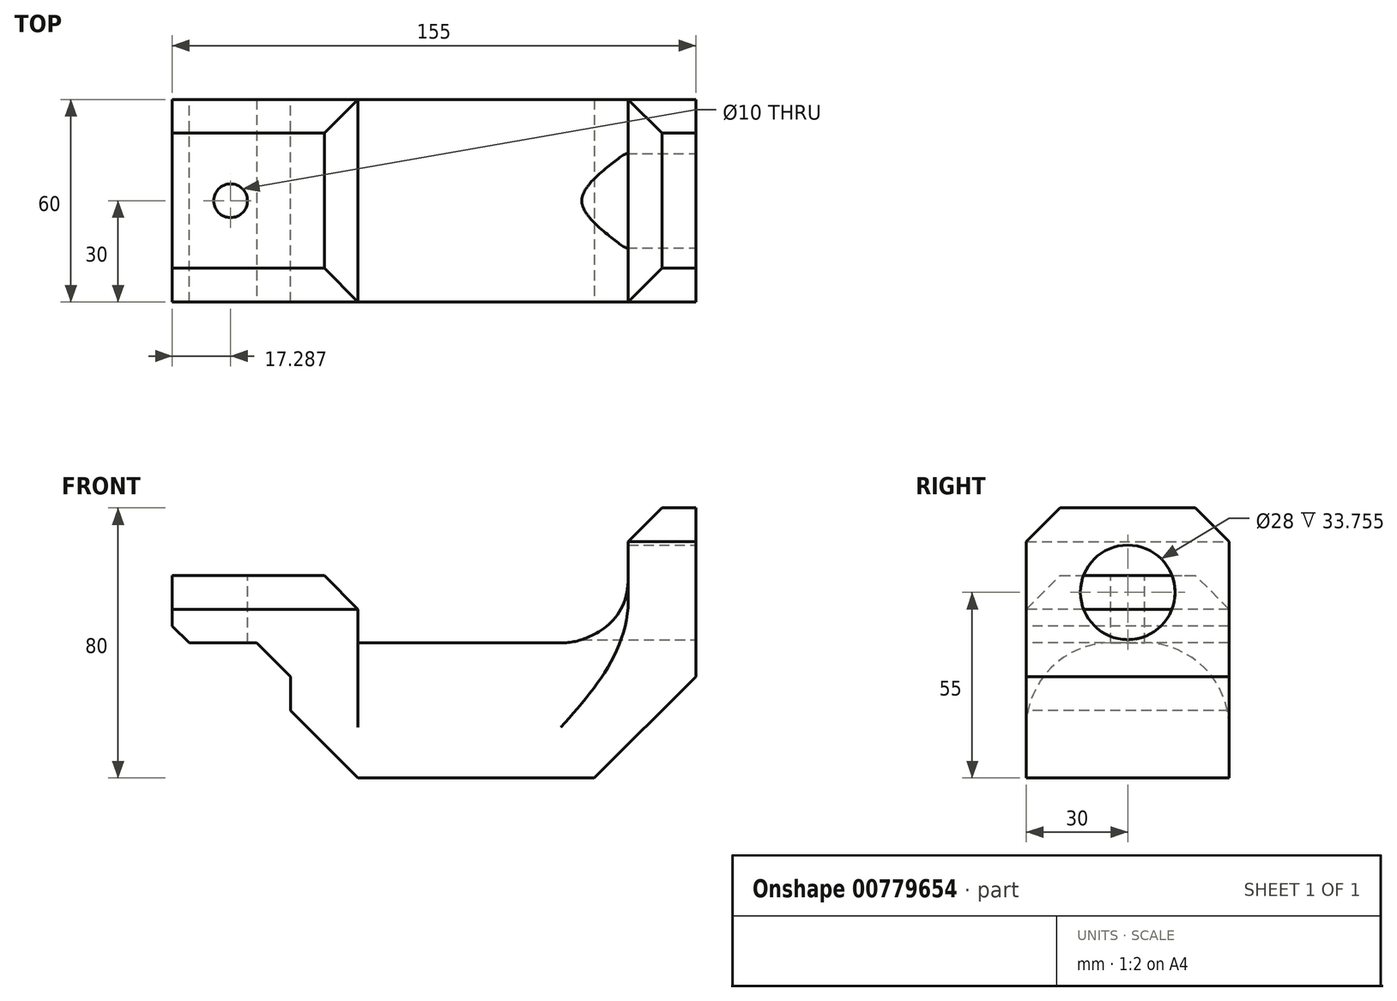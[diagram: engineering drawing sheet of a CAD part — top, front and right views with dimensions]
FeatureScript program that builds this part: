
annotation { "Feature Type Name" : "Feature", "Feature Type Description" : "" }
export const myFeature = defineFeature(function(context is Context, id is Id, definition is map)
    precondition{}
    {
        {
            var Q0;
            Q0=qCreatedBy(makeId("Front.planeOp"),FACE);
            var sketch = newSketch(context, id + "F0", { "sketchPlane" : qUnion([Q0])});
            skLineSegment(sketch, "E0.bottom", {"start": v(40, 20) * mm, "end": v(-40, 20) * mm});
            skLineSegment(sketch, "E0.top", {"start": v(40, -20) * mm, "end": v(-40, -20) * mm});
            skLineSegment(sketch, "E0.left", {"start": v(40, 20) * mm, "end": v(40, -20) * mm});
            skLineSegment(sketch, "E0.right", {"start": v(-40, 20) * mm, "end": v(-40, -20) * mm});
            skPoint(sketch, "E0.middle", {"position": v(0, 0) * mm});
            skLineSegment(sketch, "E1.bottom", {"start": v(-40, -20) * mm, "end": v(-60, -20) * mm});
            skLineSegment(sketch, "E1.top", {"start": v(-40, 40) * mm, "end": v(-60, 40) * mm});
            skLineSegment(sketch, "E1.left", {"start": v(-40, -20) * mm, "end": v(-40, 40) * mm});
            skLineSegment(sketch, "E1.right", {"start": v(-60, -20) * mm, "end": v(-60, 40) * mm});
            skLineSegment(sketch, "E2.bottom", {"start": v(-60, 40) * mm, "end": v(-80, 40) * mm});
            skLineSegment(sketch, "E2.top", {"start": v(-60, 20) * mm, "end": v(-80, 20) * mm});
            skLineSegment(sketch, "E2.left", {"start": v(-60, 40) * mm, "end": v(-60, 20) * mm});
            skLineSegment(sketch, "E3.bottom", {"start": v(-80, 40) * mm, "end": v(-95, 40) * mm});
            skLineSegment(sketch, "E3.top", {"start": v(-80, 20) * mm, "end": v(-95, 20) * mm});
            skLineSegment(sketch, "E3.right", {"start": v(-95, 40) * mm, "end": v(-95, 20) * mm});
            skLineSegment(sketch, "E4.bottom", {"start": v(40, -20) * mm, "end": v(60, -20) * mm});
            skLineSegment(sketch, "E4.top", {"start": v(40, 60) * mm, "end": v(60, 60) * mm});
            skLineSegment(sketch, "E4.left", {"start": v(40, -20) * mm, "end": v(40, 60) * mm});
            skLineSegment(sketch, "E4.right", {"start": v(60, -20) * mm, "end": v(60, 60) * mm});
            skSolve(sketch);
        }
        {
            var Q0;
            Q0 = qSketchRegion(id + "F0", true);
            extrude(context, id + "F1", {"entities" : qUnion([Q0]), "depth" : 60 * mm, "offsetDistance" : 25 * mm});
        }
        {
            var Q0;
            Q0=makeQuery(id+"F1.opExtrude","CAP_EDGE",EDGE,{"disambiguationData":[OSD([sQuery(id+"F0.wireOp",EDGE,"E0.bottom")])],"isStart":false});
            var Q1;
            Q1=makeQuery(id+"F1.opExtrude","CAP_EDGE",EDGE,{"disambiguationData":[OSD([sQuery(id+"F0.wireOp",EDGE,"E0.bottom")])],"isStart":true});
            fillet(context, id + "F2", {"entities" : qUnion([Q0, Q1]), "radius" : 25 * mm, "tangentPropagation" : true, "allowEdgeOverflow" : false});
        }
        {
            var Q0;
            Q0=makeQuery(id+"F1.opExtrude","SWEPT_FACE",FACE,{"disambiguationData":[OSD([sQuery(id+"F0.wireOp",EDGE,"E1.top"),sQuery(id+"F0.wireOp",EDGE,"E2.bottom"),sQuery(id+"F0.wireOp",EDGE,"E3.bottom")])]});
            var sketch = newSketch(context, id + "F3", { "sketchPlane" : qUnion([Q0])});
            skLineSegment(sketch, "E5", {"start": v(-60.43, -60) * mm, "end": v(-95, 0) * mm});
            skLineSegment(sketch, "E6", {"start": v(-95, 0) * mm, "end": v(-60.43, -60) * mm});
            skLineSegment(sketch, "E7", {"start": v(-60.43, 0) * mm, "end": v(-95, -60) * mm});
            skPoint(sketch, "E8", {"position": v(-77.71, -30) * mm});
            skSolve(sketch);
        }
        {
            var Q0;
            Q0=sQuery(id+"F3.wireOp",VERTEX,"E8");
            var Q1;
            Q1=makeQuery(id+"F1.opExtrude","SWEPT_BODY",BODY,{"disambiguationData":[OSD([sQuery(id+"F0.wireOp",EDGE,"E0.bottom"),sQuery(id+"F0.wireOp",EDGE,"E0.top"),sQuery(id+"F0.wireOp",EDGE,"E1.bottom"),sQuery(id+"F0.wireOp",EDGE,"E1.top"),sQuery(id+"F0.wireOp",EDGE,"E1.left"),sQuery(id+"F0.wireOp",EDGE,"E1.right"),sQuery(id+"F0.wireOp",EDGE,"E2.bottom"),sQuery(id+"F0.wireOp",EDGE,"E2.top"),sQuery(id+"F0.wireOp",EDGE,"E3.bottom"),sQuery(id+"F0.wireOp",EDGE,"E3.top"),sQuery(id+"F0.wireOp",EDGE,"E3.right"),sQuery(id+"F0.wireOp",EDGE,"E4.bottom"),sQuery(id+"F0.wireOp",EDGE,"E4.top"),sQuery(id+"F0.wireOp",EDGE,"E4.left"),sQuery(id+"F0.wireOp",EDGE,"E4.right")])]});
            hole(context, id + "F4", {"style" : HoleStyle.SIMPLE, "endStyle" : HoleEndStyle.THROUGH, "holeDiameter" : 10 * mm, "majorDiameter" : 5 * mm, "isTappedThrough" : true, "tappedDepth" : 12 * mm, "tapClearance" : 3, "locations" : qUnion([Q0]), "scope" : qUnion([Q1])});
        }
        {
            var Q0;
            Q0=makeQuery(id+"F1.opExtrude","SWEPT_EDGE",EDGE,{"disambiguationData":[OSD([sQuery(id+"F0.wireOp",EDGE,"E0.bottom"),sQuery(id+"F0.wireOp",EDGE,"E4.left")])]});
            fillet(context, id + "F5", {"entities" : qUnion([Q0]), "radius" : 20 * mm, "tangentPropagation" : true, "allowEdgeOverflow" : false});
        }
        {
            var Q0;
            Q0=makeQuery(id+"F1.opExtrude","CAP_EDGE",EDGE,{"disambiguationData":[OSD([sQuery(id+"F0.wireOp",EDGE,"E1.top"),sQuery(id+"F0.wireOp",EDGE,"E2.bottom"),sQuery(id+"F0.wireOp",EDGE,"E3.bottom")])],"isStart":false});
            var Q1;
            Q1=makeQuery(id+"F1.opExtrude","CAP_EDGE",EDGE,{"disambiguationData":[OSD([sQuery(id+"F0.wireOp",EDGE,"E1.top"),sQuery(id+"F0.wireOp",EDGE,"E2.bottom"),sQuery(id+"F0.wireOp",EDGE,"E3.bottom")])],"isStart":true});
            var Q2;
            Q2=makeQuery(id+"F1.opExtrude","CAP_EDGE",EDGE,{"disambiguationData":[OSD([sQuery(id+"F0.wireOp",EDGE,"E4.top")])],"isStart":false});
            var Q3;
            Q3=makeQuery(id+"F1.opExtrude","CAP_EDGE",EDGE,{"disambiguationData":[OSD([sQuery(id+"F0.wireOp",EDGE,"E4.top")])],"isStart":true});
            var Q4;
            Q4=makeQuery(id+"F1.opExtrude","SWEPT_EDGE",EDGE,{"disambiguationData":[OSD([sQuery(id+"F0.wireOp",EDGE,"E1.top"),sQuery(id+"F0.wireOp",EDGE,"E1.left")])]});
            var Q5;
            Q5=makeQuery(id+"F1.opExtrude","SWEPT_EDGE",EDGE,{"disambiguationData":[OSD([sQuery(id+"F0.wireOp",EDGE,"E4.top"),sQuery(id+"F0.wireOp",EDGE,"E4.left")])]});
            chamfer(context, id + "F6", {"entities" : qUnion([Q0, Q1, Q2, Q3, Q4, Q5]), "width" : 10 * mm, "tangentPropagation" : true});
        }
        {
            var Q0;
            Q0=makeQuery(id+"F1.opExtrude","SWEPT_EDGE",EDGE,{"disambiguationData":[OSD([sQuery(id+"F0.wireOp",EDGE,"E4.bottom"),sQuery(id+"F0.wireOp",EDGE,"E4.right")])]});
            chamfer(context, id + "F7", {"entities" : qUnion([Q0]), "width" : 30 * mm, "tangentPropagation" : true});
        }
        {
            var Q0;
            Q0=makeQuery(id+"F1.opExtrude","SWEPT_EDGE",EDGE,{"disambiguationData":[OSD([sQuery(id+"F0.wireOp",EDGE,"E1.bottom"),sQuery(id+"F0.wireOp",EDGE,"E1.right")])]});
            chamfer(context, id + "F8", {"entities" : qUnion([Q0]), "width" : 20 * mm, "tangentPropagation" : true});
        }
        {
            var Q0;
            Q0=makeQuery(id+"F1.opExtrude","SWEPT_FACE",FACE,{"disambiguationData":[OSD([sQuery(id+"F0.wireOp",EDGE,"E4.right")])]});
            var sketch = newSketch(context, id + "F9", { "sketchPlane" : qUnion([Q0])});
            skPoint(sketch, "E9", {"position": v(-30, 35) * mm});
            skPoint(sketch, "E9.positionSnap0", {"position": v(-30, 60) * mm});
            skSolve(sketch);
        }
        {
            var Q0;
            Q0=sQuery(id+"F9.wireOp",VERTEX,"E9");
            var Q1;
            Q1=makeQuery(id+"F1.opExtrude","SWEPT_BODY",BODY,{"disambiguationData":[OSD([sQuery(id+"F0.wireOp",EDGE,"E0.bottom"),sQuery(id+"F0.wireOp",EDGE,"E0.top"),sQuery(id+"F0.wireOp",EDGE,"E1.bottom"),sQuery(id+"F0.wireOp",EDGE,"E1.top"),sQuery(id+"F0.wireOp",EDGE,"E1.left"),sQuery(id+"F0.wireOp",EDGE,"E1.right"),sQuery(id+"F0.wireOp",EDGE,"E2.bottom"),sQuery(id+"F0.wireOp",EDGE,"E2.top"),sQuery(id+"F0.wireOp",EDGE,"E3.bottom"),sQuery(id+"F0.wireOp",EDGE,"E3.top"),sQuery(id+"F0.wireOp",EDGE,"E3.right"),sQuery(id+"F0.wireOp",EDGE,"E4.bottom"),sQuery(id+"F0.wireOp",EDGE,"E4.top"),sQuery(id+"F0.wireOp",EDGE,"E4.left"),sQuery(id+"F0.wireOp",EDGE,"E4.right")])]});
            hole(context, id + "F10", {"style" : HoleStyle.SIMPLE, "endStyle" : HoleEndStyle.BLIND, "holeDiameter" : 28 * mm, "majorDiameter" : 5 * mm, "holeDepth" : 50 * mm, "isTappedThrough" : true, "tappedDepth" : 12 * mm, "tapClearance" : 3, "locations" : qUnion([Q0]), "scope" : qUnion([Q1])});
        }
        {
            var Q0;
            Q0=makeQuery(id+"F1.opExtrude","SWEPT_EDGE",EDGE,{"disambiguationData":[OSD([sQuery(id+"F0.wireOp",EDGE,"E3.top"),sQuery(id+"F0.wireOp",EDGE,"E3.right")])]});
            chamfer(context, id + "F11", {"entities" : qUnion([Q0]), "width" : 5 * mm, "tangentPropagation" : true});
        }
        {
            var Q0;
            Q0=makeQuery(id+"F1.opExtrude","SWEPT_EDGE",EDGE,{"disambiguationData":[OSD([sQuery(id+"F0.wireOp",EDGE,"E1.right"),sQuery(id+"F0.wireOp",EDGE,"E2.top"),sQuery(id+"F0.wireOp",EDGE,"E2.left")])]});
            chamfer(context, id + "F12", {"entities" : qUnion([Q0]), "width" : 10 * mm, "tangentPropagation" : true});
        }
    });
